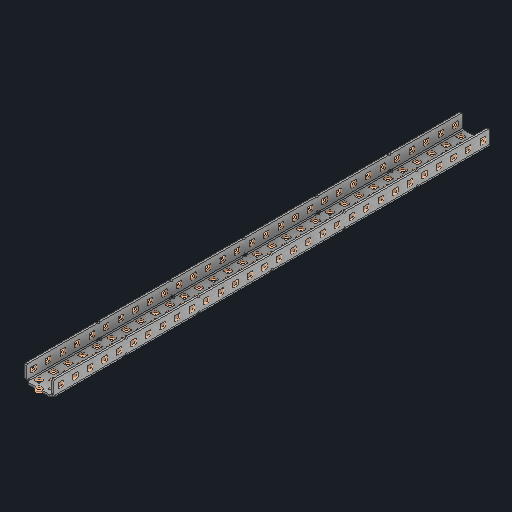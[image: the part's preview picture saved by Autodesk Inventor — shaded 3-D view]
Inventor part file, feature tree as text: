
AUTODESK INVENTOR PART (.ipt)
format: ipt  version: 2025 (Build 290162000, 162)  size: 2,435,584 bytes
history: native  units: in
note: dims shown in document units (in); Inventor stores cm internally (conversion verified against a paired STEP export)
features: other x306, sketch x5, sheet_metal_op x1
ambient origin geometry x8: Origin, YZ Plane, XZ Plane, XY Plane, X Axis, Y Axis, Z Axis, Center Point
bodies: Solid1 (feature_tree)
feature tree (312):
  other  "Alu C 1x2x1x30.ipt"
  other  "Solid1::Alu C 1x2x1x30.ipt"
  other  "TaggingFeature1"
  sketch  "Sketch1"  dims[d0=0.3937in]
  sketch  "Sketch2"  dims[d1=0.0625in]
  sketch  "Sketch3"
  other  "Flange Pattern Sketch"
  sketch  "Sketch9"
  sheet_metal_op  "Body Pattern Sketch"
  other  "Arc Length"
  sketch  "Sketch14"
  other  "Flange Pattern Plane"
  other  "Srf1"
  other  "Srf2"
  other  "Srf3"
  other  "Srf4"
  other  "Srf5"
  other  "Srf6"
  other  "Srf7"
  other  "Srf8"
  other  "Srf9"
  other  "Srf10"
  other  "Srf11"
  other  "Srf12"
  other  "Srf13"
  other  "Srf14"
  other  "Srf15"
  other  "Srf16"
  other  "Srf17"
  other  "Srf18"
  other  "Srf19"
  other  "Srf20"
  other  "Srf21"
  other  "Srf22"
  other  "Srf23"
  other  "Srf24"
  other  "Srf25"
  other  "Srf26"
  other  "Srf27"
  other  "Srf28"
  other  "Srf29"
  other  "Srf30"
  other  "Srf31"
  other  "Srf32"
  other  "Srf33"
  other  "Srf34"
  other  "Srf35"
  other  "Srf36"
  other  "Srf37"
  other  "Srf38"
  other  "Srf39"
  other  "Srf40"
  other  "Srf41"
  other  "Srf42"
  other  "Srf43"
  other  "Srf44"
  other  "Srf45"
  other  "Srf46"
  other  "Srf47"
  other  "Srf48"
  other  "Srf49"
  other  "Srf50"
  other  "Srf51"
  other  "Srf52"
  other  "Srf53"
  other  "Srf54"
  other  "Srf55"
  other  "Srf56"
  other  "Srf57"
  other  "Srf58"
  other  "Srf59"
  other  "Srf60"
  other  "Srf61"
  other  "Srf62"
  other  "Srf63"
  other  "Srf64"
  other  "Srf65"
  other  "Srf66"
  other  "Srf67"
  other  "Srf68"
  other  "Srf69"
  other  "Srf70"
  other  "Srf71"
  other  "Srf72"
  other  "Srf73"
  other  "Srf74"
  other  "Srf75"
  other  "Srf76"
  other  "Srf77"
  other  "Srf78"
  other  "Srf79"
  other  "Srf80"
  other  "Srf81"
  other  "Srf82"
  other  "Srf83"
  other  "Srf84"
  other  "Srf85"
  other  "Srf86"
  other  "Srf87"
  other  "Srf88"
  other  "Srf89"
  other  "Srf90"
  other  "Srf91"
  other  "Srf92"
  other  "Srf93"
  other  "Srf94"
  other  "Srf95"
  other  "Srf96"
  other  "Srf97"
  other  "Srf98"
  other  "Srf99"
  other  "Srf100"
  other  "Srf101"
  other  "Srf102"
  other  "Srf103"
  other  "Srf104"
  other  "Srf105"
  other  "Srf106"
  other  "Srf107"
  other  "Srf108"
  other  "Srf109"
  other  "Srf110"
  other  "Srf111"
  other  "Srf112"
  other  "Srf113"
  other  "Srf114"
  other  "Srf115"
  other  "Srf116"
  other  "Srf117"
  other  "Srf118"
  other  "Srf119"
  other  "Srf120"
  other  "Srf121"
  other  "Srf122"
  other  "Srf123"
  other  "Srf124"
  other  "Srf125"
  other  "Srf126"
  other  "Srf127"
  other  "Srf128"
  other  "Srf129"
  other  "Srf130"
  other  "Srf131"
  other  "Srf132"
  other  "Srf133"
  other  "Srf134"
  other  "Srf135"
  other  "Srf136"
  other  "Srf137"
  other  "Srf138"
  other  "Srf139"
  other  "Srf140"
  other  "Srf141"
  other  "Srf142"
  other  "Srf143"
  other  "Srf144"
  other  "Srf145"
  other  "Srf146"
  other  "Srf147"
  other  "Srf148"
  other  "Srf149"
  other  "Srf150"
  other  "Srf1::Derived"
  other  "Srf2::Derived"
  other  "Srf823::Derived"
  other  "Srf824::Derived"
  other  "Srf825::Derived"
  other  "Srf826::Derived"
  other  "Srf827::Derived"
  other  "Srf828::Derived"
  other  "Srf829::Derived"
  other  "Srf922::Derived"
  other  "Srf923::Derived"
  other  "Srf924::Derived"
  other  "Srf925::Derived"
  other  "Srf926::Derived"
  other  "Srf1143::Derived"
  other  "Srf1144::Derived"
  other  "Srf1145::Derived"
  other  "Srf1146::Derived"
  other  "Srf1147::Derived"
  other  "Srf1148::Derived"
  other  "Srf1149::Derived"
  other  "Srf1150::Derived"
  other  "Srf1151::Derived"
  other  "Srf1152::Derived"
  other  "Srf1153::Derived"
  other  "Srf1154::Derived"
  other  "Srf1155::Derived"
  other  "Srf1156::Derived"
  other  "Srf1157::Derived"
  other  "Srf1158::Derived"
  other  "Srf1159::Derived"
  other  "Srf1160::Derived"
  other  "Srf1161::Derived"
  other  "Srf1162::Derived"
  other  "Srf1163::Derived"
  other  "Srf1164::Derived"
  other  "Srf1165::Derived"
  other  "Srf1166::Derived"
  other  "Srf1167::Derived"
  other  "Srf1168::Derived"
  other  "Srf1169::Derived"
  other  "Srf1170::Derived"
  other  "Srf1171::Derived"
  other  "Srf1172::Derived"
  other  "Srf1173::Derived"
  other  "Srf1174::Derived"
  other  "Srf1175::Derived"
  other  "Srf1176::Derived"
  other  "Srf1177::Derived"
  other  "Srf1178::Derived"
  other  "Srf1179::Derived"
  other  "Srf1180::Derived"
  other  "Srf1181::Derived"
  other  "Srf1182::Derived"
  other  "Srf1183::Derived"
  other  "Srf1184::Derived"
  other  "Srf1185::Derived"
  other  "Srf1186::Derived"
  other  "Srf1187::Derived"
  other  "Srf1188::Derived"
  other  "Srf91::Derived"
  other  "Srf92::Derived"
  other  "Srf856::Derived"
  other  "Srf857::Derived"
  other  "Srf858::Derived"
  other  "Srf859::Derived"
  other  "Srf860::Derived"
  other  "Srf861::Derived"
  other  "Srf862::Derived"
  other  "Srf959::Derived"
  other  "Srf960::Derived"
  other  "Srf961::Derived"
  other  "Srf962::Derived"
  other  "Srf963::Derived"
  other  "Srf1199::Derived"
  other  "Srf1200::Derived"
  other  "Srf1201::Derived"
  other  "Srf1202::Derived"
  other  "Srf1203::Derived"
  other  "Srf1204::Derived"
  other  "Srf1205::Derived"
  other  "Srf1206::Derived"
  other  "Srf1207::Derived"
  other  "Srf1208::Derived"
  other  "Srf1209::Derived"
  other  "Srf1210::Derived"
  other  "Srf1211::Derived"
  other  "Srf1212::Derived"
  other  "Srf1213::Derived"
  other  "Srf1214::Derived"
  other  "Srf1215::Derived"
  other  "Srf1216::Derived"
  other  "Srf1217::Derived"
  other  "Srf1218::Derived"
  other  "Srf1219::Derived"
  other  "Srf1220::Derived"
  other  "Srf1221::Derived"
  other  "Srf1222::Derived"
  other  "Srf1223::Derived"
  other  "Srf1224::Derived"
  other  "Srf1225::Derived"
  other  "Srf1226::Derived"
  other  "Srf1227::Derived"
  other  "Srf1228::Derived"
  other  "Srf1229::Derived"
  other  "Srf1230::Derived"
  other  "Srf1231::Derived"
  other  "Srf1232::Derived"
  other  "Srf1233::Derived"
  other  "Srf1234::Derived"
  other  "Srf1235::Derived"
  other  "Srf1236::Derived"
  other  "Srf1237::Derived"
  other  "Srf1238::Derived"
  other  "Srf1239::Derived"
  other  "Srf1240::Derived"
  other  "Srf1241::Derived"
  other  "Srf1242::Derived"
  other  "Srf1243::Derived"
  other  "Srf1244::Derived"
  other  "Srf786::Derived"
  other  "Srf889::Derived"
  other  "Srf890::Derived"
  other  "Srf891::Derived"
  other  "Srf892::Derived"
  other  "Srf893::Derived"
  other  "Srf894::Derived"
  other  "Srf895::Derived"
  other  "Srf896::Derived"
  other  "Srf996::Derived"
  other  "Srf997::Derived"
  other  "Srf998::Derived"
  other  "Srf999::Derived"
  other  "Srf1000::Derived"
  other  "Srf1255::Derived"
  other  "Srf1256::Derived"
  other  "Srf1257::Derived"
  other  "Srf1258::Derived"
  other  "Srf1259::Derived"
  other  "Srf1260::Derived"
  other  "Srf1261::Derived"
  other  "Srf1262::Derived"
  other  "Srf1263::Derived"
  other  "Srf1264::Derived"
  other  "Srf1265::Derived"
  other  "Srf1266::Derived"
  other  "Srf1267::Derived"
  other  "Srf1268::Derived"
  other  "Srf1269::Derived"
  other  "Srf1270::Derived"
